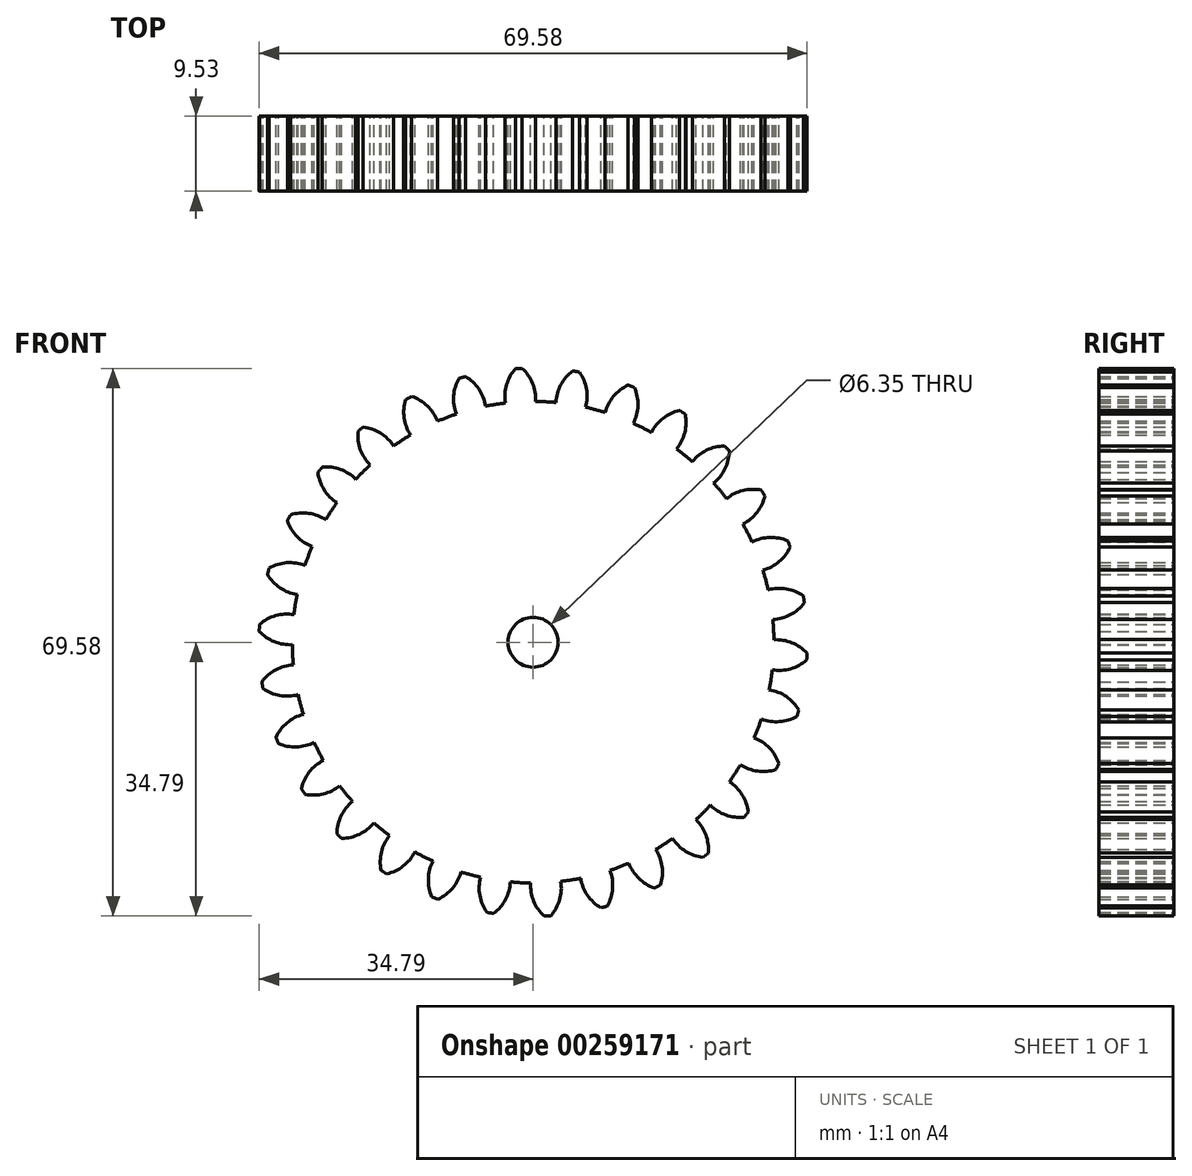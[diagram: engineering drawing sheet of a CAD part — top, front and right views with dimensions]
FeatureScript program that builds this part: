
annotation { "Feature Type Name" : "Feature", "Feature Type Description" : "" }
export const myFeature = defineFeature(function(context is Context, id is Id, definition is map)
    precondition{}
    {
        {
            var Q0;
            Q0=qCreatedBy(makeId("Front.planeOp"),FACE);
            var sketch = newSketch(context, id + "F0", { "sketchPlane" : qUnion([Q0])});
            skCircle(sketch, "E0", {"center": v(0, 0) * mm, "radius": 30.59 * mm});
            skCircle(sketch, "E1", {"center": v(0, 0) * mm, "radius": 32.7 * mm, "construction": true});
            skCircle(sketch, "E2", {"center": v(0, 0) * mm, "radius": 34.82 * mm, "construction": true});
            skLineSegment(sketch, "E3", {"start": v(0, 34.82) * mm, "end": v(0, 0) * mm, "construction": true});
            skLineSegment(sketch, "E4", {"start": v(0, 32.7) * mm, "end": v(-38.93, 32.7) * mm, "construction": true});
            skLineSegment(sketch, "E5", {"start": v(0, 32.7) * mm, "end": v(-39.73, 18.24) * mm, "construction": true});
            skLineSegment(sketch, "E6", {"start": v(0, 0) * mm, "end": v(-1.82, 34.77) * mm, "construction": true});
            skArc(sketch, "E7", {"start": v(0, 32.7) * mm, "mid": v(-0.57, 33.83) * mm, "end": v(-1.4, 34.8) * mm});
            skArc(sketch, "E8", {"start": v(-1.4, 34.8) * mm, "mid": v(-1.82, 34.77) * mm, "end": v(-2.25, 34.75) * mm});
            skPoint(sketch, "E9", {"position": v(0, 32.7) * mm});
            skPoint(sketch, "E10", {"position": v(-1.71, 32.66) * mm});
            skArc(sketch, "E11", {"start": v(0.27, 31.64) * mm, "mid": v(-0.3, 33.36) * mm, "end": v(-1.4, 34.8) * mm});
            skCircle(sketch, "E12", {"center": v(0, 0) * mm, "radius": 31.65 * mm, "construction": true});
            skArc(sketch, "E13.MirrorCS", {"start": v(-3.57, 31.44) * mm, "mid": v(-3.2, 33.21) * mm, "end": v(-2.25, 34.75) * mm});
            skArc(sketch, "E14", {"start": v(-2.25, 34.75) * mm, "mid": v(-3.37, 32.7) * mm, "end": v(-3.5, 30.39) * mm});
            skArc(sketch, "E15", {"start": v(0.31, 30.59) * mm, "mid": v(-0.07, 32.88) * mm, "end": v(-1.4, 34.8) * mm});
            skCircle(sketch, "E16", {"center": v(0, 0) * mm, "radius": 3.18 * mm});
            skSolve(sketch);
        }
        {
            var Q0;
            Q0 = qSketchRegion(id + "F0", true);
            extrude(context, id + "F1", {"entities" : qUnion([Q0]), "depth" : 9.52 * mm});
        }
        {
            var Q0;
            Q0=makeQuery(id+"F1.opExtrude","SWEPT_BODY",BODY,{"disambiguationData":[OSD([sQuery(id+"F0.wireOp",EDGE,"E0"),sQuery(id+"F0.wireOp",EDGE,"E7"),sQuery(id+"F0.wireOp",EDGE,"d04c000b-2145-497f-91d3-6f61c6da05620.MirrorCS"),sQuery(id+"F0.wireOp",EDGE,"E8")])]});
            var Q1;
            Q1=makeQuery(id+"F1.opExtrude","SWEPT_FACE",FACE,{"disambiguationData":[OSD([sQuery(id+"F0.wireOp",EDGE,"E8")])]});
            var Q2;
            Q2=makeQuery(id+"F1.opExtrude","SWEPT_FACE",FACE,{"disambiguationData":[OSD([sQuery(id+"F0.wireOp",EDGE,"E15")])]});
            var Q3;
            Q3=makeQuery(id+"F1.opExtrude","SWEPT_FACE",FACE,{"disambiguationData":[OSD([sQuery(id+"F0.wireOp",EDGE,"E14")])]});
            var Q4;
            Q4=makeQuery(id+"F1.opExtrude","SWEPT_FACE",FACE,{"disambiguationData":[OSD([sQuery(id+"F0.wireOp",EDGE,"E0")])]});
            circularPattern(context, id + "F2", {"patternType" : PatternType.FACE, "faces" : qUnion([Q1, Q2, Q3]), "axis" : qUnion([Q4]), "angle" : 360 * degree, "instanceCount" : 30, "equalSpace" : true});
        }
    });
